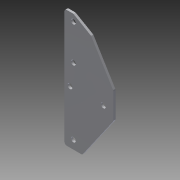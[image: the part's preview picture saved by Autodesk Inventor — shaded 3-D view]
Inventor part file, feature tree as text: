
AUTODESK INVENTOR PART (.ipt)
format: ipt  version: 2014 SP1 (Build 180222100, 222)  size: 154,624 bytes
history: native  units: in
note: dims shown in document units (in); Inventor stores cm internally (conversion verified against a paired STEP export)
features: extrude x6, sketch x6, fillet x5
ambient origin geometry x8: Origin, YZ Plane, XZ Plane, XY Plane, X Axis, Y Axis, Z Axis, Center Point
bodies: Solid1 (feature_tree)
feature tree (17):
  extrude  "Extrusion1"  Depth=0.125in TaperAngle=0.0deg
  extrude  "Extrusion2"  Depth=0.28in
  extrude  "Extrusion3"  Depth=0.5in
  fillet  "Fillet2"  Radius=0.56in
  fillet  "Fillet3"  Radius=0.31in
  extrude  "Extrusion4"  Depth=0.266in
  extrude  "Extrusion5"  Depth=0.5in
  fillet  "Fillet4"  Radius=0.5in
  extrude  "Extrusion6"  Depth=0.125in
  fillet  "Fillet5"  Radius=1.0in
  fillet  "Fillet6"  Radius=0.125in
  sketch  "Sketch1"  dims[d1=1.5in d3=0.125in d4=0.0in]
  sketch  "Sketch2"  dims[d5=0.28in d6=0.28in]
  sketch  "Sketch3"  dims[d7=0.5in d8=0.5in d9=0.56in d11=0.31in]
  sketch  "Sketch4"  dims[d12=1.0in d13=0.0in d15=0.266in]
  sketch  "Sketch5"  dims[d16=0.266in d17=0.5in d18=0.5in]
  sketch  "Sketch6"  dims[d19=1.737in d20=2.0in d21=1.0in d22=0.0in d23=0.125in d24=2.5in d25=2.75in d26=2.75in d27=0.125in d28=0.266in d29=3.75in d30=0.5in d31=1.0in d32=0.0in d33=1.0in d34=0.0in d36=4.125in d38=0.8344in d39=0.125in d40=30.0deg d41=0.5in d42=1.0in d43=0.0in d44=0.125in d45=1.0in d46=0.125in]
